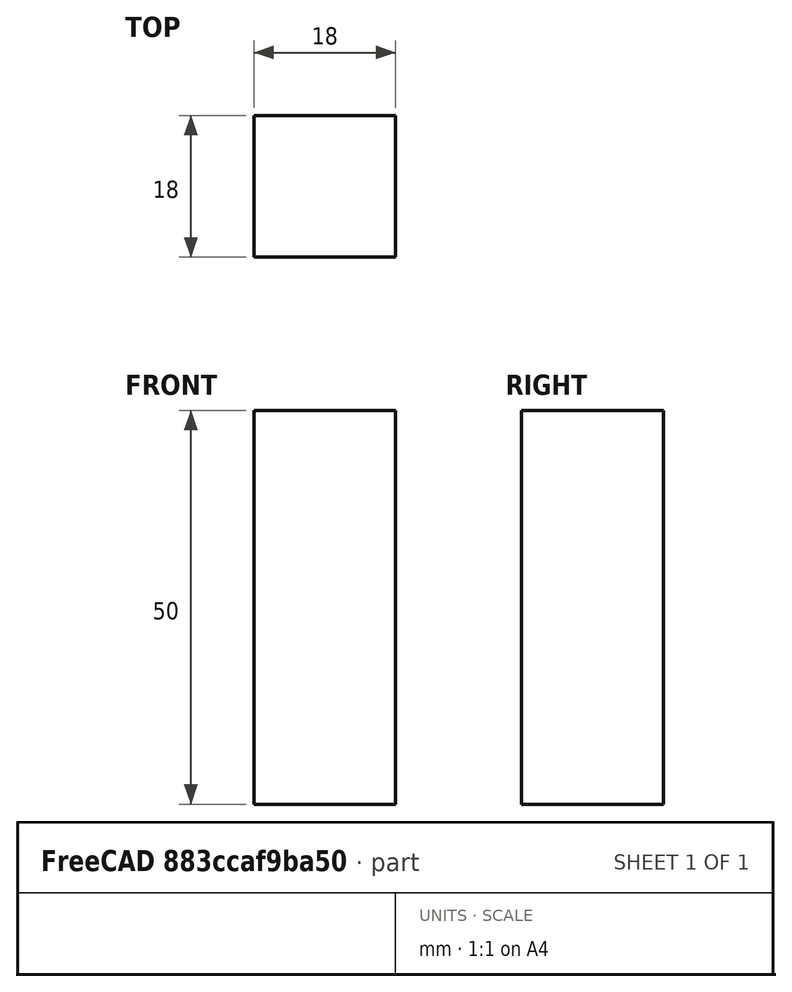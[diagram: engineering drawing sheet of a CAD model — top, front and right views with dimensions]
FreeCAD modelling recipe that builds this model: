
FCSTD DOCUMENT  (FreeCAD 0.15R4671 (Git))
Label: Square Bar 18 EN10059 S235JR
License: All rights reserved
LicenseURL: http://en.wikipedia.org/wiki/All_rights_reserved
objects: Sketcher::SketchObject×1, Part::Extrusion×1
note: 2 computed .brp shape members not serialized (recipe doc carries the construction recipe); baked Part::Feature solids carry a one-line shape summary decoded from their .brp

FEATURE [Sketcher::SketchObject] Sketch
  sketch-geometry (4):
    g0: LineSegment StartX=-9 StartY=-9 StartZ=0 EndX=9 EndY=-9 EndZ=0
    g1: LineSegment StartX=9 StartY=-9 StartZ=0 EndX=9 EndY=9 EndZ=0
    g2: LineSegment StartX=9 StartY=9 StartZ=0 EndX=-9 EndY=9 EndZ=0
    g3: LineSegment StartX=-9 StartY=9 StartZ=0 EndX=-9 EndY=-9 EndZ=0
  constraints (12):
    c: Coincident(g0,g1)
    c: Coincident(g1,g2)
    c: Coincident(g2,g3)
    c: Coincident(g3,g0)
    c: Horizontal(g0)
    c: Horizontal(g2)
    c: Vertical(g1)
    c: Vertical(g3)
    c: Symmetric(g1,g0,g-1)
    c: Symmetric(g2,g1,g-2)
    c: Equal(g1,g2)
    c: DistanceY(g1) = 18
FEATURE [Part::Extrusion] Extrude  label="Square Bar 18 EN10059 S235JR"
  Base = -> Sketch
  Dir = (0,0,50)
  Solid = true
